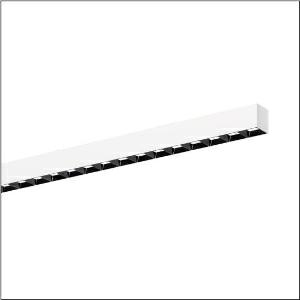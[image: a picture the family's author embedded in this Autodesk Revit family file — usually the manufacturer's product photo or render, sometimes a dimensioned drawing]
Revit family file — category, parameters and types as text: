
# Revit family: silica_r__21_51mx22tat4w_9510
name_source: partatom
category: Lighting Fixtures
units: mm (PartAtom-declared; Revit-internal decimal feet)

## family parameters
Cut with Voids When Loaded = No
Host = Face
Light Source = No
Part Type = Normal
Room Calculation Point = No
Round Connector Dimension = Use Diameter
Shared = No

## types (1)
- --- (1 x LED, 3720 lm, 32.1 W, 6500K)
    Apparent Load = 32 VA
    CIE Flux Codes = 84 100 100 100 100
    Color Rendering = 80
    Color Temperature = 6500K
    Default Elevation = 1800 mm
    Description = Silica® 21, office luminaire, primary light control with darklight reflector, of PMMA, black, CAT 2 (L<= 3000cd/m²), light emission: direct distribution, primary light characteristic: symmetric, installation type: surface-mounted, LED, rated luminous flux: 3.720lm, luminous efficacy: 110lm/W, light colour: 8tw, colour temperature: 2700..6500K, control gear: ECG DALI, with terminal, 3+2-pole, max. 2.5mm², mains connection: 220..240V, AC, 50/60Hz, rated input power: 33.8W, luminaire housing, of aluminium, traffic white (RAL 9016), length: 1.204mm, width: 53mm, height: 53mm, protection rating (complete): IP20, insulation class (complete): insulation class I (protective earthing), certification: CE, permissible operating ambient temperature: 0..+35°C, standard: EN 50419, packaging unit: 1 piece
    Height = 0 mm  [stored 0 ft]
    Lamp = 1 x LED
    Lamp Light Flux = 3720 lm
    Lamp Power = 32.1 W
    Lamp count = 1
    Length = 1204 mm
    Luminous efficacy = 116 lm/W
    Manufacturer = Siteco
    ModVariant = No
    Model = 51MX22TAT4W
    Mounting Place = Ceiling
    Mounting Type = Recessed
    Number of Poles = 1
    OnlyDefault = Yes
    Power Factor = 1
    Product Name = Silica® 21
    Product group = office luminaire | ceiling recessed
    ProductGroupID = 401
    Protection Class = Protection class I
    Protection Degree = IP 20
    RLX_Detail_Level = 1
    RLX_Emergency_Light_Flux = 0 lm
    RLX_Emergency_Type = 0
    RLX_Emergency_Type_DB = No
    RlxData = <blob elided: 37953 chars, md5=9fbc6d3d>
    Socket = socket
    Standby Power = 0 W
    System Light Flux = 3720 lm
    System Power = 32 W
    Type Comments = individual setting
    Type Image = l_1297779.jpg
    URL = http://relux.com
    VarID = @adj_071485
    Voltage = 0 V
    Weight = 0.00 kg
    Width = 53 mm

note: [stored X ft] marks values corroborated as IEEE doubles in the binary element streams (Revit-internal decimal feet)

## geometry (parser evidence)
native form markers: Blend x4, Sweep x10
no freeform markers — native parametric forms only
